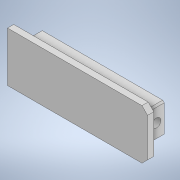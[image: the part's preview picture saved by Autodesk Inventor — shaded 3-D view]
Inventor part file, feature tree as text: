
AUTODESK INVENTOR PART (.ipt)
format: ipt  version: 2021 (Build 250183000, 183)  size: 130,048 bytes
history: native  units: mm
features: extrude x3, sketch x3, mirror x1, chamfer x1, projected_geometry x1
ambient origin geometry x8: Origin, YZ Plane, XZ Plane, XY Plane, X Axis, Y Axis, Z Axis, Center Point
bodies: Solid1 (feature_tree)
feature tree (9):
  extrude  "Extrusion1"  Depth=9.7mm
  extrude  "Extrusion2"  Depth=16.0mm
  extrude  "Extrusion3"  Depth=2.0mm
  mirror  "Mirror1"
  chamfer  "Chamfer1"  Distance=1.8mm
  sketch  "Sketch1"  dims[d0=39.7mm d1=9.7mm]
  sketch  "Sketch2"  dims[d2=6.0mm d3=0.0mm d8=16.0mm]
  projected_geometry  "Projected Loop1"
  sketch  "Sketch3"  dims[d9=45.0mm d10=22.5mm d11=1.8mm d12=1.8mm d13=2.0mm d14=0.0mm d15=3.5mm d16=2.8mm d17=10.0mm d18=0.0mm d19=0.5mm d20=2.0mm d21=45.0deg]
